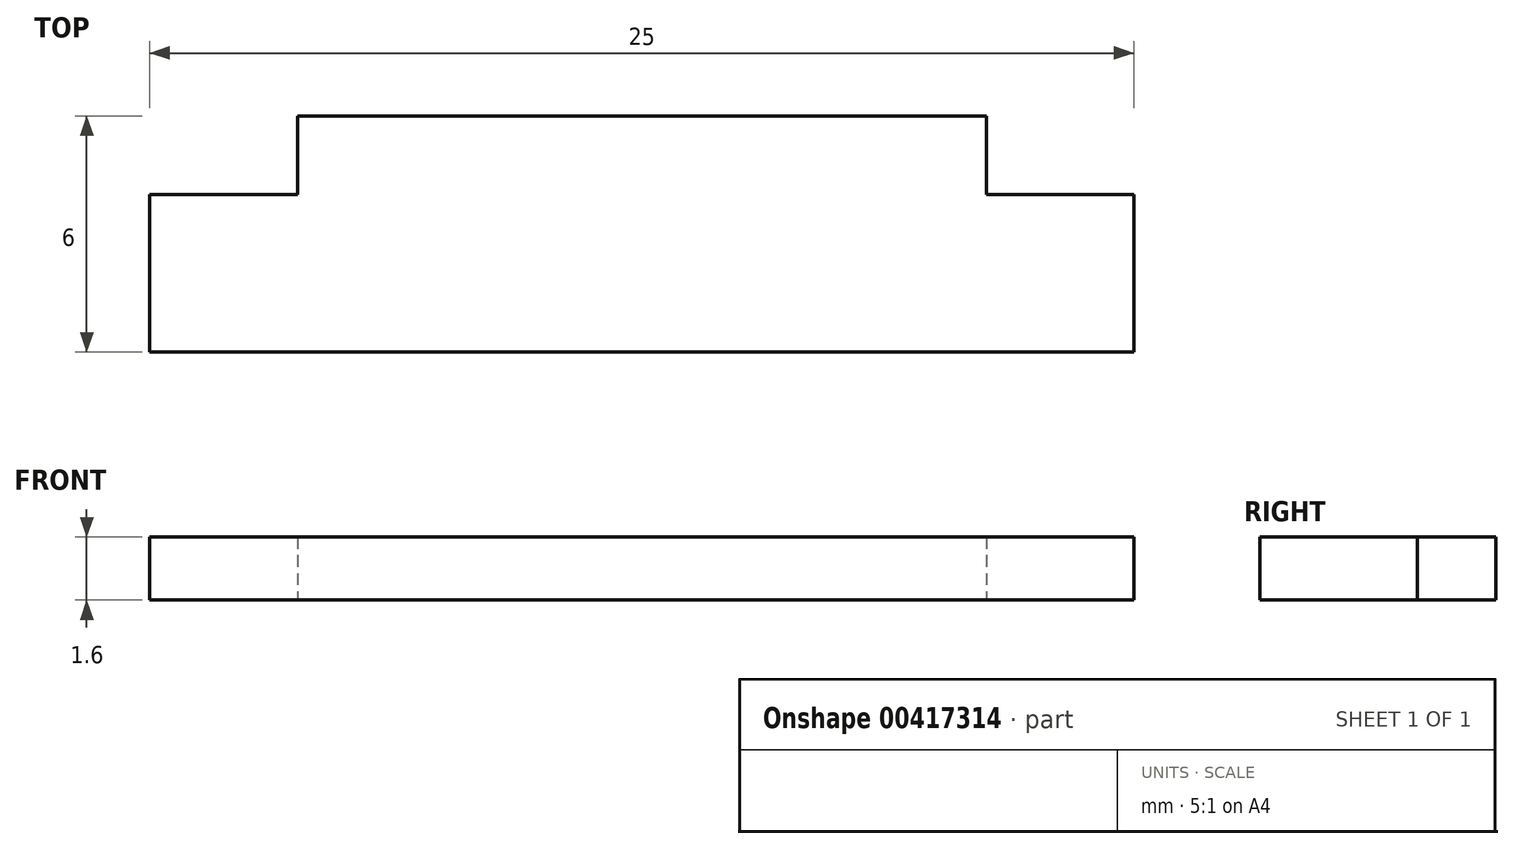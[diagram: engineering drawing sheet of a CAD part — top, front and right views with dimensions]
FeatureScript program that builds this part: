
annotation { "Feature Type Name" : "Feature", "Feature Type Description" : "" }
export const myFeature = defineFeature(function(context is Context, id is Id, definition is map)
    precondition{}
    {
        {
            var Q0;
            Q0=qCreatedBy(makeId("Top.planeOp"),FACE);
            var sketch = newSketch(context, id + "F0", { "sketchPlane" : qUnion([Q0])});
            skLineSegment(sketch, "E0.bottom", {"start": v(8.75, 2) * mm, "end": v(-8.75, 2) * mm});
            skLineSegment(sketch, "E0.top", {"start": v(8.75, -2) * mm, "end": v(-8.75, -2) * mm});
            skLineSegment(sketch, "E0.left", {"start": v(8.75, 2) * mm, "end": v(8.75, -2) * mm});
            skLineSegment(sketch, "E0.right", {"start": v(-8.75, 2) * mm, "end": v(-8.75, -2) * mm});
            skPoint(sketch, "E0.middle", {"position": v(0, 0) * mm});
            skLineSegment(sketch, "E1.bottom", {"start": v(-8.75, -2) * mm, "end": v(-12.5, -2) * mm});
            skLineSegment(sketch, "E1.top", {"start": v(-8.75, 2) * mm, "end": v(-12.5, 2) * mm});
            skLineSegment(sketch, "E1.left", {"start": v(-8.75, -2) * mm, "end": v(-8.75, 2) * mm});
            skLineSegment(sketch, "E1.right", {"start": v(-12.5, -2) * mm, "end": v(-12.5, 2) * mm});
            skLineSegment(sketch, "E2.bottom", {"start": v(8.75, -2) * mm, "end": v(12.5, -2) * mm});
            skLineSegment(sketch, "E2.top", {"start": v(8.75, 2) * mm, "end": v(12.5, 2) * mm});
            skLineSegment(sketch, "E2.left", {"start": v(8.75, -2) * mm, "end": v(8.75, 2) * mm});
            skLineSegment(sketch, "E2.right", {"start": v(12.5, -2) * mm, "end": v(12.5, 2) * mm});
            skSolve(sketch);
        }
        {
            var Q0;
            Q0=makeQuery(id+"F0.imprint","IMPRINT",FACE,{"disambiguationData":[TD([[makeQuery(id+"F0.imprint","IMPRINT",EDGE,{"derivedFrom":sQuery(id+"F0.wireOp",EDGE,"E0.bottom")}),1.0]])]});
            extrude(context, id + "F1", {"entities" : qUnion([Q0]), "depth" : 1.6 * mm});
        }
        {
            var Q0;
            Q0=makeQuery(id+"F0.imprint","IMPRINT",FACE,{"disambiguationData":[TD([[makeQuery(id+"F0.imprint","IMPRINT",EDGE,{"derivedFrom":sQuery(id+"F0.wireOp",EDGE,"E1.bottom")}),-1.0]])]});
            var Q1;
            Q1=makeQuery(id+"F0.imprint","IMPRINT",FACE,{"disambiguationData":[TD([[makeQuery(id+"F0.imprint","IMPRINT",EDGE,{"derivedFrom":sQuery(id+"F0.wireOp",EDGE,"E2.bottom")}),1.0]])]});
            var Q2;
            Q2=makeQuery(id+"F1.opExtrude","CAP_FACE",FACE,{"disambiguationData":[OSD([sQuery(id+"F0.wireOp",EDGE,"E0.bottom"),sQuery(id+"F0.wireOp",EDGE,"E0.top"),sQuery(id+"F0.wireOp",EDGE,"E1.left"),sQuery(id+"F0.wireOp",EDGE,"E2.left")])],"isStart":false});
            extrude(context, id + "F2", {"entities" : qUnion([Q0, Q1]), "endBound" : BoundingType.UP_TO_SURFACE, "endBoundEntityFace" : qUnion([Q2]), "depth" : 25 * mm});
        }
        {
            var Q0;
            Q0=makeQuery(id+"F1.opExtrude","SWEPT_FACE",FACE,{"disambiguationData":[OSD([sQuery(id+"F0.wireOp",EDGE,"E0.bottom")])]});
            extrude(context, id + "F3", {"entities" : qUnion([Q0]), "operationType" : NewBodyOperationType.ADD, "depth" : 2 * mm});
        }
    });
